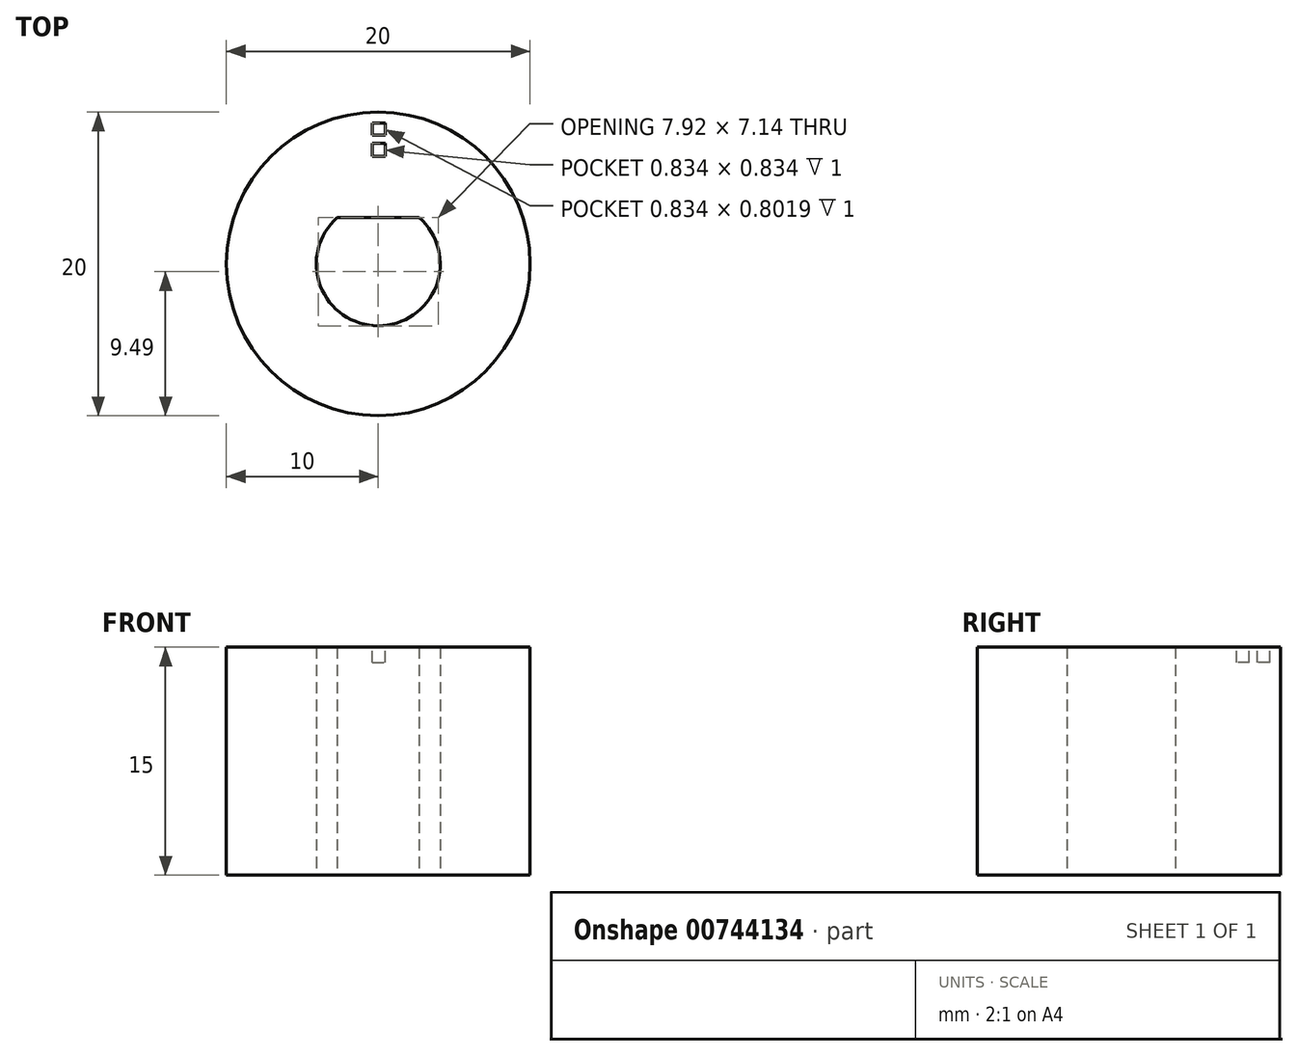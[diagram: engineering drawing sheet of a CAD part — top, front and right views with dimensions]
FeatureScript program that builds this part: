
annotation { "Feature Type Name" : "Feature", "Feature Type Description" : "" }
export const myFeature = defineFeature(function(context is Context, id is Id, definition is map)
    precondition{}
    {
        {
            var Q0;
            Q0=qCreatedBy(makeId("Top.planeOp"),FACE);
            var sketch = newSketch(context, id + "F0", { "sketchPlane" : qUnion([Q0])});
            skArc(sketch, "E0", {"start": v(-2.7, 3.06) * mm, "mid": v(0, -4.08) * mm, "end": v(2.7, 3.06) * mm});
            skCircle(sketch, "E1", {"center": v(0, 0) * mm, "radius": 10 * mm});
            skLineSegment(sketch, "E2", {"start": v(-2.7, 3.06) * mm, "end": v(2.7, 3.06) * mm});
            skSolve(sketch);
        }
        {
            var Q0;
            Q0=makeQuery(id+"F0.imprint","IMPRINT",FACE,{"disambiguationData":[TD([[makeQuery(id+"F0.imprint","IMPRINT",EDGE,{"derivedFrom":sQuery(id+"F0.wireOp",EDGE,"E0")}),-1.0]])]});
            extrude(context, id + "F1", {"entities" : qUnion([Q0]), "depth" : 15 * mm, "offsetDistance" : 25 * mm});
        }
        {
            var Q0;
            Q0=makeQuery(id+"F1.opExtrude","CAP_FACE",FACE,{"disambiguationData":[OSD([sQuery(id+"F0.wireOp",EDGE,"E0"),sQuery(id+"F0.wireOp",EDGE,"E1"),sQuery(id+"F0.wireOp",EDGE,"E2")])],"isStart":false});
            var sketch = newSketch(context, id + "F2", { "sketchPlane" : qUnion([Q0])});
            skLineSegment(sketch, "E3.bottom", {"start": v(-0.38, 9.27) * mm, "end": v(0.46, 9.27) * mm});
            skLineSegment(sketch, "E3.top", {"start": v(-0.38, 8.47) * mm, "end": v(0.46, 8.47) * mm});
            skLineSegment(sketch, "E3.left", {"start": v(-0.38, 9.27) * mm, "end": v(-0.38, 8.47) * mm});
            skLineSegment(sketch, "E3.right", {"start": v(0.46, 9.27) * mm, "end": v(0.46, 8.47) * mm});
            skLineSegment(sketch, "E4.bottom", {"start": v(-0.38, 7.93) * mm, "end": v(0.46, 7.93) * mm});
            skLineSegment(sketch, "E4.top", {"start": v(-0.38, 7.1) * mm, "end": v(0.46, 7.1) * mm});
            skLineSegment(sketch, "E4.left", {"start": v(-0.38, 7.93) * mm, "end": v(-0.38, 7.1) * mm});
            skLineSegment(sketch, "E4.right", {"start": v(0.46, 7.93) * mm, "end": v(0.46, 7.1) * mm});
            skSolve(sketch);
        }
        {
            var Q0;
            Q0=makeQuery(id+"F2.imprint","IMPRINT",FACE,{"disambiguationData":[TD([[makeQuery(id+"F2.imprint","IMPRINT",EDGE,{"derivedFrom":sQuery(id+"F2.wireOp",EDGE,"E3.bottom")}),-1.0]])]});
            var Q1;
            Q1=makeQuery(id+"F2.imprint","IMPRINT",FACE,{"disambiguationData":[TD([[makeQuery(id+"F2.imprint","IMPRINT",EDGE,{"derivedFrom":sQuery(id+"F2.wireOp",EDGE,"E4.bottom")}),-1.0]])]});
            extrude(context, id + "F3", {"entities" : qUnion([Q0, Q1]), "operationType" : NewBodyOperationType.REMOVE, "oppositeDirection" : true, "depth" : 1 * mm, "offsetDistance" : 25 * mm});
        }
    });
